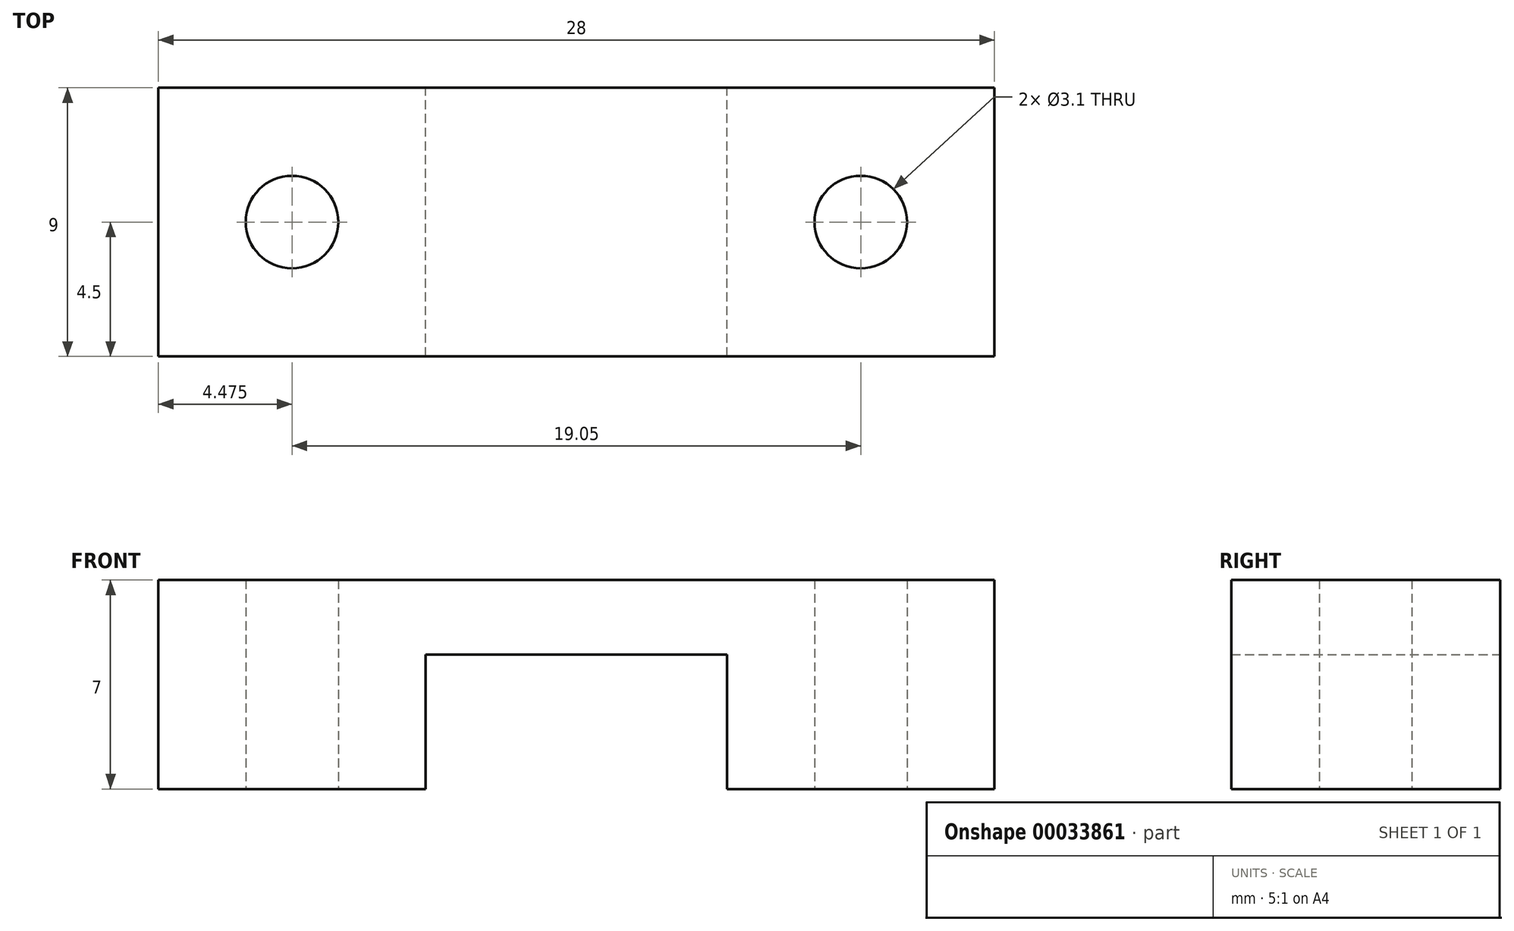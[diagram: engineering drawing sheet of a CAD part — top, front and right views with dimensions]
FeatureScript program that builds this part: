
annotation { "Feature Type Name" : "Feature", "Feature Type Description" : "" }
export const myFeature = defineFeature(function(context is Context, id is Id, definition is map)
    precondition{}
    {
        {
            var Q0;
            Q0=qCreatedBy(makeId("Front.planeOp"),FACE);
            var sketch = newSketch(context, id + "F0", { "sketchPlane" : qUnion([Q0])});
            skLineSegment(sketch, "E0.rect.bottom", {"start": v(14, -3.5) * mm, "end": v(-14, -3.5) * mm, "construction": true});
            skLineSegment(sketch, "E0.rect.top", {"start": v(14, 3.5) * mm, "end": v(-14, 3.5) * mm, "construction": true});
            skLineSegment(sketch, "E0.rect.left", {"start": v(14, -3.5) * mm, "end": v(14, 3.5) * mm, "construction": true});
            skLineSegment(sketch, "E0.rect.right", {"start": v(-14, -3.5) * mm, "end": v(-14, 3.5) * mm, "construction": true});
            skPoint(sketch, "E0.rect.middle", {"position": v(0, 0) * mm});
            skLineSegment(sketch, "E1", {"start": v(-14, 1) * mm, "end": v(14, 1) * mm, "construction": true});
            skLineSegment(sketch, "E2", {"start": v(5.05, 3.5) * mm, "end": v(5.05, -3.5) * mm, "construction": true});
            skLineSegment(sketch, "E3", {"start": v(0, 3.5) * mm, "end": v(14, 3.5) * mm});
            skLineSegment(sketch, "E4", {"start": v(14, -3.5) * mm, "end": v(14, 3.5) * mm});
            skLineSegment(sketch, "E5", {"start": v(14, -3.5) * mm, "end": v(5.05, -3.5) * mm});
            skLineSegment(sketch, "E6", {"start": v(5.05, 1) * mm, "end": v(0, 1) * mm});
            skLineSegment(sketch, "E7", {"start": v(5.05, 1) * mm, "end": v(5.05, -3.5) * mm});
            skLineSegment(sketch, "E8.MirrorCS", {"start": v(0, 3.5) * mm, "end": v(-14, 3.5) * mm});
            skLineSegment(sketch, "E9.MirrorCS", {"start": v(-14, -3.5) * mm, "end": v(-14, 3.5) * mm});
            skLineSegment(sketch, "E10.MirrorCS", {"start": v(-14, -3.5) * mm, "end": v(-5.05, -3.5) * mm});
            skLineSegment(sketch, "E11.MirrorCS", {"start": v(-5.05, 1) * mm, "end": v(-5.05, -3.5) * mm});
            skLineSegment(sketch, "E12.MirrorCS", {"start": v(-5.05, 1) * mm, "end": v(0, 1) * mm});
            skLineSegment(sketch, "E13", {"start": v(9.52, -3.5) * mm, "end": v(9.52, 3.5) * mm, "construction": true});
            skLineSegment(sketch, "E14", {"start": v(8.03, 3.5) * mm, "end": v(8.03, -3.5) * mm, "construction": true});
            skLineSegment(sketch, "E15.MirrorCS", {"start": v(11.02, 3.5) * mm, "end": v(11.02, -3.5) * mm, "construction": true});
            skSolve(sketch);
        }
        {
            var Q0;
            Q0=makeQuery(id+"F0.imprint","IMPRINT",FACE,{"disambiguationData":[TD([[makeQuery(id+"F0.imprint","IMPRINT",EDGE,{"derivedFrom":sQuery(id+"F0.wireOp",EDGE,"E3")}),-1.0]])]});
            extrude(context, id + "F1", {"entities" : qUnion([Q0]), "endBound" : BoundingType.SYMMETRIC, "depth" : 9 * mm});
        }
        {
            var Q0;
            Q0=makeQuery(id+"F1.opExtrude","SWEPT_FACE",FACE,{"disambiguationData":[OSD([sQuery(id+"F0.wireOp",EDGE,"E5")])]});
            var sketch = newSketch(context, id + "F2", { "sketchPlane" : qUnion([Q0])});
            skLineSegment(sketch, "E16", {"start": v(9.52, -4.5) * mm, "end": v(9.52, 4.5) * mm, "construction": true});
            skCircle(sketch, "E17", {"center": v(9.52, 0) * mm, "radius": 1.55 * mm});
            skCircle(sketch, "E18.MirrorC", {"center": v(-9.53, 0) * mm, "radius": 1.55 * mm});
            skSolve(sketch);
        }
        {
            var Q0;
            Q0=qSketchRegion(id+"F2",true);
            extrude(context, id + "F3", {"entities" : qUnion([Q0]), "operationType" : NewBodyOperationType.REMOVE, "endBound" : BoundingType.UP_TO_NEXT, "oppositeDirection" : true, "depth" : 25 * mm});
        }
    });
